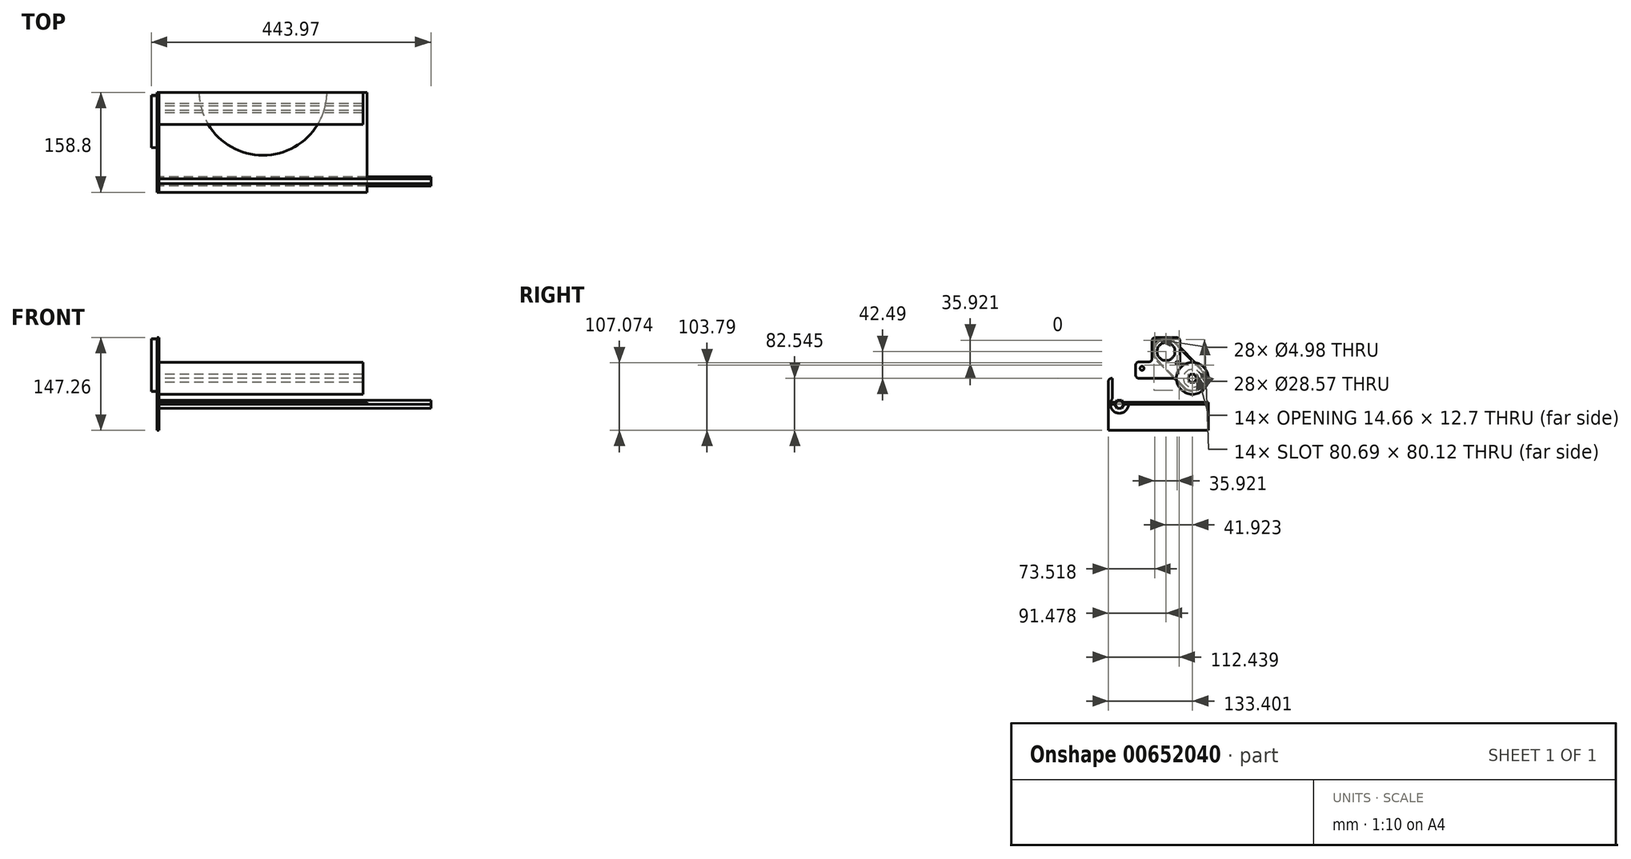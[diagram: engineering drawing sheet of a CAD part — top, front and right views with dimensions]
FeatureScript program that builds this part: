
annotation { "Feature Type Name" : "Feature", "Feature Type Description" : "" }
export const myFeature = defineFeature(function(context is Context, id is Id, definition is map)
    precondition{}
    {
        {
            var Q0;
            Q0=qCreatedBy(makeId("Top.planeOp"),FACE);
            var sketch = newSketch(context, id + "F0", { "sketchPlane" : qUnion([Q0])});
            skLineSegment(sketch, "E0.bottom", {"start": v(-165.1, 82.55) * mm, "end": v(165.1, 82.55) * mm});
            skLineSegment(sketch, "E0.top", {"start": v(-165.1, -82.55) * mm, "end": v(165.1, -82.55) * mm});
            skLineSegment(sketch, "E0.left", {"start": v(-165.1, 82.55) * mm, "end": v(-165.1, -82.55) * mm});
            skLineSegment(sketch, "E0.right", {"start": v(165.1, 82.55) * mm, "end": v(165.1, -82.55) * mm});
            skPoint(sketch, "E0.middle", {"position": v(0, 0) * mm});
            skLineSegment(sketch, "E1.top", {"start": v(-165.1, 31.75) * mm, "end": v(165.1, 31.75) * mm});
            skLineSegment(sketch, "E1.left", {"start": v(-165.1, 82.55) * mm, "end": v(-165.1, 31.75) * mm});
            skLineSegment(sketch, "E1.right", {"start": v(165.1, 82.55) * mm, "end": v(165.1, 31.75) * mm});
            skLineSegment(sketch, "E2.bottom", {"start": v(-165.1, -76.2) * mm, "end": v(-158.75, -76.2) * mm});
            skLineSegment(sketch, "E2.top", {"start": v(-165.1, -47.63) * mm, "end": v(-158.75, -47.63) * mm});
            skLineSegment(sketch, "E2.left", {"start": v(-165.1, -76.2) * mm, "end": v(-165.1, -47.63) * mm});
            skLineSegment(sketch, "E2.right", {"start": v(-158.75, -76.2) * mm, "end": v(-158.75, -47.63) * mm});
            skLineSegment(sketch, "E3", {"start": v(-165.1, 57.15) * mm, "end": v(165.1, 57.15) * mm, "construction": true});
            skLineSegment(sketch, "E4", {"start": v(-165.1, -61.91) * mm, "end": v(165.1, -61.91) * mm, "construction": true});
            skCircle(sketch, "E5", {"center": v(0, 77.79) * mm, "radius": 139.7 * mm, "construction": true});
            skCircle(sketch, "E6", {"center": v(0, 77.79) * mm, "radius": 101.6 * mm});
            skLineSegment(sketch, "E7.bottom", {"start": v(-165.1, 76.25) * mm, "end": v(-147.4, 76.25) * mm});
            skLineSegment(sketch, "E7.top", {"start": v(-165.1, 38.05) * mm, "end": v(-147.4, 38.05) * mm});
            skLineSegment(sketch, "E7.left", {"start": v(-165.1, 76.25) * mm, "end": v(-165.1, 38.05) * mm});
            skLineSegment(sketch, "E7.right", {"start": v(-147.4, 76.25) * mm, "end": v(-147.4, 38.05) * mm});
            skPoint(sketch, "E7.middle", {"position": v(-156.25, 57.15) * mm});
            skLineSegment(sketch, "E8", {"start": v(-165.1, 76.25) * mm, "end": v(165.1, 76.25) * mm});
            skSolve(sketch);
        }
        {
            var Q0;
            {var subQ0=sQuery(id+"F0.wireOp",EDGE,"E7.top");Q0=makeQuery(id+"F0.imprint","IMPRINT",FACE,{"disambiguationData":[TD([[makeQuery(id+"F0.imprint","IMPRINT",EDGE,{"derivedFrom":subQ0}),-1.0]])]});}
            var Q1;
            Q1=makeQuery(id+"F0.imprint","IMPRINT",FACE,{"disambiguationData":[TD([[makeQuery(id+"F0.imprint","IMPRINT",EDGE,{"derivedFrom":sQuery(id+"F0.wireOp",EDGE,"E7.top")}),1.0]])]});
            var Q2;
            {var subQ1=sQuery(id+"F0.wireOp",EDGE,"E1.top");var subQ3=sQuery(id+"F0.wireOp",EDGE,"E6");var subQ4=makeQuery(id+"F0.imprint","INTERSECT",VERTEX,{"disambiguationData":[OD(1.0)],"derivedFrom":[subQ1,subQ3]});Q2=makeQuery(id+"F0.imprint","IMPRINT",FACE,{"disambiguationData":[TD([[makeQuery(id+"F0.imprint","IMPRINT",EDGE,{"disambiguationData":[TD([[subQ4,-1.0]])],"derivedFrom":subQ3}),-1.0]])]});}
            var Q3;
            {var subQ3=sQuery(id+"F0.wireOp",EDGE,"E0.top");Q3=makeQuery(id+"F0.imprint","IMPRINT",FACE,{"disambiguationData":[TD([[makeQuery(id+"F0.imprint","IMPRINT",EDGE,{"derivedFrom":subQ3}),1.0]])]});}
            var Q4;
            Q4=makeQuery(id+"F0.imprint","IMPRINT",FACE,{"disambiguationData":[TD([[makeQuery(id+"F0.imprint","IMPRINT",EDGE,{"derivedFrom":sQuery(id+"F0.wireOp",EDGE,"E2.bottom")}),1.0]])]});
            extrude(context, id + "F1", {"entities" : qUnion([Q0, Q1, Q2, Q3, Q4]), "depth" : 3.17 * mm, "offsetDistance" : 25.4 * mm});
        }
        {
            var Q0;
            Q0=makeQuery(id+"F1.opExtrude","SWEPT_FACE",FACE,{"disambiguationData":[OSD([sQuery(id+"F0.wireOp",EDGE,"E0.left"),sQuery(id+"F0.wireOp",EDGE,"E1.left"),sQuery(id+"F0.wireOp",EDGE,"E2.left")])]});
            var sketch = newSketch(context, id + "F2", { "sketchPlane" : qUnion([Q0])});
            skLineSegment(sketch, "E9.bottom", {"start": v(-76.25, 41.28) * mm, "end": v(76.25, 41.28) * mm});
            skLineSegment(sketch, "E9.top", {"start": v(-76.25, -41.28) * mm, "end": v(76.25, -41.28) * mm});
            skLineSegment(sketch, "E9.left", {"start": v(-76.25, 41.28) * mm, "end": v(-76.25, -41.28) * mm});
            skLineSegment(sketch, "E9.right", {"start": v(76.25, 41.28) * mm, "end": v(76.25, -41.28) * mm});
            skPoint(sketch, "E9.middle", {"position": v(0, 0) * mm});
            skCircle(sketch, "E10", {"center": v(-50.85, 41.28) * mm, "radius": 25.4 * mm});
            skCircle(sketch, "E11", {"center": v(-50.85, 41.28) * mm, "radius": 14.29 * mm});
            skLineSegment(sketch, "E12.bottom", {"start": v(76.25, 41.28) * mm, "end": v(82.55, 41.28) * mm});
            skLineSegment(sketch, "E12.top", {"start": v(76.25, -41.28) * mm, "end": v(82.55, -41.28) * mm});
            skLineSegment(sketch, "E12.left", {"start": v(76.25, 41.27) * mm, "end": v(76.25, -41.28) * mm});
            skLineSegment(sketch, "E12.right", {"start": v(82.55, 41.28) * mm, "end": v(82.55, -41.27) * mm});
            skCircle(sketch, "E13", {"center": v(65.09, 0) * mm, "radius": 14.29 * mm});
            skCircle(sketch, "E14", {"center": v(-8.93, 83.76) * mm, "radius": 25.4 * mm, "construction": true});
            skCircle(sketch, "E15", {"center": v(9.03, 101.73) * mm, "radius": 2.49 * mm});
            skLineSegment(sketch, "E16", {"start": v(-8.93, 83.76) * mm, "end": v(-26.89, 101.73) * mm, "construction": true});
            skLineSegment(sketch, "E17", {"start": v(-8.93, 83.76) * mm, "end": v(9.03, 101.73) * mm, "construction": true});
            skCircle(sketch, "E18.MirrorC", {"center": v(-26.89, 65.8) * mm, "radius": 2.49 * mm});
            skCircle(sketch, "E19", {"center": v(-8.93, 83.76) * mm, "radius": 14.29 * mm});
            skCircle(sketch, "E20", {"center": v(29.17, 57.15) * mm, "radius": 3.18 * mm});
            skLineSegment(sketch, "E21.bottom", {"start": v(13.3, 41.28) * mm, "end": v(45.05, 41.28) * mm});
            skLineSegment(sketch, "E21.top", {"start": v(13.3, 73.02) * mm, "end": v(45.05, 73.02) * mm});
            skLineSegment(sketch, "E21.left", {"start": v(13.3, 41.28) * mm, "end": v(13.3, 73.02) * mm});
            skLineSegment(sketch, "E22", {"start": v(-8.93, 83.76) * mm, "end": v(-8.93, 109.16) * mm, "construction": true});
            skLineSegment(sketch, "E23.bottom", {"start": v(-31.15, 105.99) * mm, "end": v(13.3, 105.99) * mm});
            skLineSegment(sketch, "E23.top", {"start": v(-31.15, 61.54) * mm, "end": v(13.3, 61.54) * mm});
            skLineSegment(sketch, "E23.left", {"start": v(-31.15, 105.99) * mm, "end": v(-31.15, 61.54) * mm});
            skLineSegment(sketch, "E23.right", {"start": v(13.3, 105.99) * mm, "end": v(13.3, 61.54) * mm});
            skLineSegment(sketch, "E24", {"start": v(-31.15, 61.54) * mm, "end": v(-31.15, 41.28) * mm});
            skLineSegment(sketch, "E25", {"start": v(13.3, 73.02) * mm, "end": v(13.3, 61.54) * mm});
            skLineSegment(sketch, "E26", {"start": v(13.3, 67.28) * mm, "end": v(39.3, 67.28) * mm});
            skLineSegment(sketch, "E27", {"start": v(39.3, 67.28) * mm, "end": v(39.3, 41.28) * mm});
            skSolve(sketch);
        }
        {
            var Q0;
            {var subQ11=sQuery(id+"F2.wireOp",EDGE,"qfJLn3O9-GlWD-lMOJ-bS2u-81kLyVJAWFBw.top");Q0=makeQuery(id+"F2.imprint","IMPRINT",FACE,{"disambiguationData":[TD([[makeQuery(id+"F2.imprint","IMPRINT",EDGE,{"derivedFrom":subQ11}),-1.0]])]});}
            var Q1;
            {var subQ0=sQuery(id+"F2.wireOp",EDGE,"E10");var subQ1=sQuery(id+"F2.wireOp",EDGE,"E9.bottom");var subQ5=makeQuery(id+"F2.imprint","INTERSECT",VERTEX,{"derivedFrom":[subQ1,subQ0]});Q1=makeQuery(id+"F2.imprint","IMPRINT",FACE,{"disambiguationData":[TD([[makeQuery(id+"F2.imprint","IMPRINT",EDGE,{"disambiguationData":[TD([[subQ5,1.0]])],"derivedFrom":subQ1}),-1.0]])]});}
            var Q2;
            {var subQ0=sQuery(id+"F2.wireOp",EDGE,"E10");var subQ1=sQuery(id+"F2.wireOp",EDGE,"E9.bottom");var subQ5=makeQuery(id+"F2.imprint","INTERSECT",VERTEX,{"derivedFrom":[subQ1,subQ0]});Q2=makeQuery(id+"F2.imprint","IMPRINT",FACE,{"disambiguationData":[TD([[makeQuery(id+"F2.imprint","IMPRINT",EDGE,{"disambiguationData":[TD([[subQ5,1.0]])],"derivedFrom":subQ1}),1.0]])]});}
            var Q3;
            {var subQ5=sQuery(id+"F2.wireOp",EDGE,"E9.top");Q3=makeQuery(id+"F2.imprint","IMPRINT",FACE,{"disambiguationData":[TD([[makeQuery(id+"F2.imprint","IMPRINT",EDGE,{"derivedFrom":subQ5}),1.0]])]});}
            var Q4;
            {var subQ5=sQuery(id+"F2.wireOp",EDGE,"E12.bottom");Q4=makeQuery(id+"F2.imprint","IMPRINT",FACE,{"disambiguationData":[TD([[makeQuery(id+"F2.imprint","IMPRINT",EDGE,{"derivedFrom":subQ5}),-1.0]])]});}
            var Q5;
            {var subQ7=sQuery(id+"F2.wireOp",EDGE,"E12.top");Q5=makeQuery(id+"F2.imprint","IMPRINT",FACE,{"disambiguationData":[TD([[makeQuery(id+"F2.imprint","IMPRINT",EDGE,{"derivedFrom":subQ7}),1.0]])]});}
            var Q6;
            Q6=makeQuery(id+"F2.imprint","IMPRINT",FACE,{"disambiguationData":[TD([[makeQuery(id+"F2.imprint","IMPRINT",EDGE,{"derivedFrom":sQuery(id+"F2.wireOp",EDGE,"E20")}),-1.0]])]});
            var Q7;
            {var subQ3=sQuery(id+"F2.wireOp",EDGE,"E21.left");Q7=makeQuery(id+"F2.imprint","IMPRINT",FACE,{"disambiguationData":[TD([[makeQuery(id+"F2.imprint","IMPRINT",EDGE,{"derivedFrom":subQ3}),1.0]])]});}
            var Q8;
            {var subQ1=sQuery(id+"F2.wireOp",EDGE,"qfJLn3O9-GlWD-lMOJ-bS2u-81kLyVJAWFBw.bottom");Q8=makeQuery(id+"F2.imprint","IMPRINT",FACE,{"disambiguationData":[TD([[makeQuery(id+"F2.imprint","IMPRINT",EDGE,{"derivedFrom":subQ1}),-1.0]])]});}
            var Q9;
            {var subQ0=sQuery(id+"F2.wireOp",EDGE,"E9.left");var subQ1=sQuery(id+"F0.wireOp",EDGE,"E7.left");var subQ2=sQuery(id+"F0.wireOp",EDGE,"E2.left");var subQ3=sQuery(id+"F0.wireOp",EDGE,"E1.left");var subQ4=sQuery(id+"F0.wireOp",EDGE,"E0.left");var subQ5=makeQuery(id+"F1.opExtrude","CAP_EDGE",EDGE,{"disambiguationData":[OSD([subQ4,subQ3,subQ2,subQ1])],"isStart":true});var subQ6=makeQuery(id+"F2.imprint","INTERSECT",VERTEX,{"derivedFrom":[subQ5,subQ0]});Q9=makeQuery(id+"F2.imprint","IMPRINT",FACE,{"disambiguationData":[TD([[makeQuery(id+"F2.imprint","IMPRINT",EDGE,{"disambiguationData":[TD([[subQ6,1.0]])],"derivedFrom":subQ0}),1.0]])]});}
            var Q10;
            {var subQ0=sQuery(id+"F2.wireOp",EDGE,"E12.right");var subQ1=sQuery(id+"F0.wireOp",EDGE,"E7.left");var subQ2=sQuery(id+"F0.wireOp",EDGE,"E2.left");var subQ3=sQuery(id+"F0.wireOp",EDGE,"E1.left");var subQ4=sQuery(id+"F0.wireOp",EDGE,"E0.left");var subQ5=makeQuery(id+"F1.opExtrude","CAP_EDGE",EDGE,{"disambiguationData":[OSD([subQ4,subQ3,subQ2,subQ1])],"isStart":true});var subQ6=makeQuery(id+"F2.imprint","INTERSECT",VERTEX,{"derivedFrom":[subQ5,subQ0]});Q10=makeQuery(id+"F2.imprint","IMPRINT",FACE,{"disambiguationData":[TD([[makeQuery(id+"F2.imprint","IMPRINT",EDGE,{"disambiguationData":[TD([[subQ6,1.0]])],"derivedFrom":subQ0}),-1.0]])]});}
            var Q11;
            Q11=makeQuery(id+"F2.imprint","IMPRINT",FACE,{"disambiguationData":[TD([[makeQuery(id+"F2.imprint","IMPRINT",EDGE,{"derivedFrom":sQuery(id+"F2.wireOp",EDGE,"E15")}),-1.0]])]});
            var Q12;
            {var subQ8=sQuery(id+"F2.wireOp",EDGE,"E21.bottom");Q12=makeQuery(id+"F2.imprint","IMPRINT",FACE,{"disambiguationData":[TD([[makeQuery(id+"F2.imprint","IMPRINT",EDGE,{"derivedFrom":subQ8}),-1.0]])]});}
            var Q13;
            {var subQ1=sQuery(id+"F2.wireOp",EDGE,"E9.bottom");var subQ4=sQuery(id+"F2.wireOp",EDGE,"E24");var subQ5=makeQuery(id+"F2.imprint","INTERSECT",VERTEX,{"derivedFrom":[subQ1,subQ4]});Q13=makeQuery(id+"F2.imprint","IMPRINT",FACE,{"disambiguationData":[TD([[makeQuery(id+"F2.imprint","IMPRINT",EDGE,{"disambiguationData":[TD([[subQ5,1.0]])],"derivedFrom":subQ1}),1.0]])]});}
            extrude(context, id + "F3", {"entities" : qUnion([Q0, Q1, Q2, Q3, Q4, Q5, Q6, Q7, Q8, Q9, Q10, Q11, Q12, Q13]), "depth" : 3.17 * mm, "offsetDistance" : 25.4 * mm});
        }
        {
            var Q0;
            Q0=makeQuery(id+"F3.opExtrude","CAP_FACE",FACE,{"disambiguationData":[OSD([sQuery(id+"F2.wireOp",EDGE,"E9.bottom"),sQuery(id+"F2.wireOp",EDGE,"E9.top"),sQuery(id+"F2.wireOp",EDGE,"E9.left"),sQuery(id+"F2.wireOp",EDGE,"E10"),sQuery(id+"F2.wireOp",EDGE,"E11"),sQuery(id+"F2.wireOp",EDGE,"E12.bottom"),sQuery(id+"F2.wireOp",EDGE,"E12.top"),sQuery(id+"F2.wireOp",EDGE,"E12.right"),sQuery(id+"F2.wireOp",EDGE,"E13"),sQuery(id+"F2.wireOp",EDGE,"qfJLn3O9-GlWD-lMOJ-bS2u-81kLyVJAWFBw.bottom"),sQuery(id+"F2.wireOp",EDGE,"qfJLn3O9-GlWD-lMOJ-bS2u-81kLyVJAWFBw.left"),sQuery(id+"F2.wireOp",EDGE,"qfJLn3O9-GlWD-lMOJ-bS2u-81kLyVJAWFBw.right"),sQuery(id+"F2.wireOp",EDGE,"E15"),sQuery(id+"F2.wireOp",EDGE,"E18.MirrorC"),sQuery(id+"F2.wireOp",EDGE,"E19"),sQuery(id+"F2.wireOp",EDGE,"E20"),sQuery(id+"F2.wireOp",EDGE,"E21.top"),sQuery(id+"F2.wireOp",EDGE,"E21.right"),sQuery(id+"F2.wireOp",EDGE,"WHWuN5Ua-Tlyi-y9Cq-qCwo-jjhaEeOhI5ko")])],"isStart":true});
            var sketch = newSketch(context, id + "F4", { "sketchPlane" : qUnion([Q0])});
            skCircle(sketch, "E28", {"center": v(50.85, 41.28) * mm, "radius": 25.4 * mm});
            skCircle(sketch, "E29.cCircle", {"center": v(50.85, 41.28) * mm, "radius": 6.35 * mm, "construction": true});
            skLineSegment(sketch, "E29.0", {"start": v(47.18, 47.63) * mm, "end": v(54.52, 47.63) * mm});
            skLineSegment(sketch, "E29.1", {"start": v(54.52, 47.63) * mm, "end": v(58.18, 41.27) * mm});
            skLineSegment(sketch, "E29.2", {"start": v(58.18, 41.27) * mm, "end": v(54.52, 34.92) * mm});
            skLineSegment(sketch, "E29.3", {"start": v(54.52, 34.93) * mm, "end": v(47.18, 34.93) * mm});
            skLineSegment(sketch, "E29.4", {"start": v(47.18, 34.93) * mm, "end": v(43.52, 41.28) * mm});
            skLineSegment(sketch, "E29.5", {"start": v(43.52, 41.28) * mm, "end": v(47.18, 47.63) * mm});
            skPoint(sketch, "E29.0.midPoint", {"position": v(50.85, 47.62) * mm});
            skCircle(sketch, "E30.cCircle", {"center": v(-65.09, 0) * mm, "radius": 6.35 * mm, "construction": true});
            skLineSegment(sketch, "E30.0", {"start": v(-68.75, 6.35) * mm, "end": v(-61.42, 6.35) * mm});
            skLineSegment(sketch, "E30.1", {"start": v(-61.42, 6.35) * mm, "end": v(-57.76, 0) * mm});
            skLineSegment(sketch, "E30.2", {"start": v(-57.76, 0) * mm, "end": v(-61.42, -6.35) * mm});
            skLineSegment(sketch, "E30.3", {"start": v(-61.42, -6.35) * mm, "end": v(-68.75, -6.35) * mm});
            skLineSegment(sketch, "E30.4", {"start": v(-68.75, -6.35) * mm, "end": v(-72.42, 0) * mm});
            skLineSegment(sketch, "E30.5", {"start": v(-72.42, 0) * mm, "end": v(-68.75, 6.35) * mm});
            skPoint(sketch, "E30.0.midPoint", {"position": v(-65.09, 6.35) * mm});
            skSolve(sketch);
        }
        {
            var Q0;
            Q0=makeQuery(id+"F4.imprint","IMPRINT",FACE,{"disambiguationData":[TD([[makeQuery(id+"F4.imprint","IMPRINT",EDGE,{"derivedFrom":makeQuery(id+"F3.opExtrude","CAP_EDGE",EDGE,{"disambiguationData":[OSD([sQuery(id+"F2.wireOp",EDGE,"W6DhLB1R-Bibj-mR2K-u9WB-GpnqnpVcpbQg")])],"isStart":true})}),1.0]])]});
            var Q1;
            Q1=makeQuery(id+"F4.imprint","IMPRINT",FACE,{"disambiguationData":[TD([[makeQuery(id+"F4.imprint","IMPRINT",EDGE,{"derivedFrom":sQuery(id+"F4.wireOp",EDGE,"E29.0")}),1.0]])]});
            var Q2;
            {var subQ5=makeQuery(id+"F3.opExtrude","CAP_EDGE",EDGE,{"disambiguationData":[OSD([sQuery(id+"F2.wireOp",EDGE,"qPiBjacE-2YdZ-56Vs-2SOP-qVqnwwztWqQn")])],"isStart":true});Q2=makeQuery(id+"F4.imprint","IMPRINT",FACE,{"disambiguationData":[TD([[makeQuery(id+"F4.imprint","IMPRINT",EDGE,{"derivedFrom":subQ5}),1.0]])]});}
            var Q3;
            {var subQ0=sQuery(id+"F4.wireOp",EDGE,"E28");Q3=makeQuery(id+"F4.imprint","IMPRINT",FACE,{"disambiguationData":[TD([[makeQuery(id+"F4.imprint","IMPRINT",EDGE,{"disambiguationData":[OD(0.0)],"derivedFrom":subQ0}),-1.0]])]});}
            extrude(context, id + "F5", {"entities" : qUnion([Q0, Q1, Q2, Q3]), "depth" : 323.85 * mm, "offsetDistance" : 25.4 * mm});
        }
        {
            var Q0;
            Q0=makeQuery(id+"F4.imprint","IMPRINT",FACE,{"disambiguationData":[TD([[makeQuery(id+"F4.imprint","IMPRINT",EDGE,{"derivedFrom":sQuery(id+"F4.wireOp",EDGE,"E30.0")}),-1.0]])]});
            extrude(context, id + "F6", {"entities" : qUnion([Q0]), "depth" : 431.8 * mm, "offsetDistance" : 25.4 * mm});
        }
        {
            var Q0;
            Q0=makeQuery(id+"F3.opExtrude","CAP_FACE",FACE,{"disambiguationData":[OSD([sQuery(id+"F2.wireOp",EDGE,"E9.bottom"),sQuery(id+"F2.wireOp",EDGE,"E9.top"),sQuery(id+"F2.wireOp",EDGE,"E9.left"),sQuery(id+"F2.wireOp",EDGE,"E10"),sQuery(id+"F2.wireOp",EDGE,"E11"),sQuery(id+"F2.wireOp",EDGE,"E12.bottom"),sQuery(id+"F2.wireOp",EDGE,"E12.top"),sQuery(id+"F2.wireOp",EDGE,"E12.right"),sQuery(id+"F2.wireOp",EDGE,"E13"),sQuery(id+"F2.wireOp",EDGE,"E15"),sQuery(id+"F2.wireOp",EDGE,"E18.MirrorC"),sQuery(id+"F2.wireOp",EDGE,"E19"),sQuery(id+"F2.wireOp",EDGE,"E20"),sQuery(id+"F2.wireOp",EDGE,"E21.top"),sQuery(id+"F2.wireOp",EDGE,"E21.right"),sQuery(id+"F2.wireOp",EDGE,"E23.bottom"),sQuery(id+"F2.wireOp",EDGE,"E23.left"),sQuery(id+"F2.wireOp",EDGE,"E23.right"),sQuery(id+"F2.wireOp",EDGE,"E24")])],"isStart":false});
            var sketch = newSketch(context, id + "F7", { "sketchPlane" : qUnion([Q0])});
            skCircle(sketch, "E31.0", {"center": v(29.17, 57.15) * mm, "radius": 3.18 * mm});
            skPoint(sketch, "E32.0", {"position": v(13.3, 41.28) * mm});
            skArc(sketch, "E33", {"start": v(-64.45, 54.7) * mm, "mid": v(-64.27, 27.68) * mm, "end": v(-37.25, 27.86) * mm});
            skArc(sketch, "E34", {"start": v(4.67, 70.35) * mm, "mid": v(4.49, 97.36) * mm, "end": v(-22.52, 97.18) * mm});
            skLineSegment(sketch, "E35", {"start": v(-64.45, 54.7) * mm, "end": v(-22.52, 97.18) * mm});
            skLineSegment(sketch, "E36", {"start": v(-37.25, 27.86) * mm, "end": v(4.67, 70.35) * mm});
            skLineSegment(sketch, "E37.0", {"start": v(-65.59, 55.81) * mm, "end": v(-23.66, 98.3) * mm});
            skArc(sketch, "E38", {"start": v(-65.59, 55.81) * mm, "mid": v(-65.39, 26.54) * mm, "end": v(-36.11, 26.74) * mm});
            skArc(sketch, "E39", {"start": v(5.8, 69.23) * mm, "mid": v(5.61, 98.5) * mm, "end": v(-23.66, 98.3) * mm});
            skLineSegment(sketch, "E40.0", {"start": v(-36.11, 26.74) * mm, "end": v(5.8, 69.23) * mm});
            skSolve(sketch);
        }
        {
            var Q0;
            {var subQ10=sQuery(id+"F7.wireOp",EDGE,"E33");Q0=makeQuery(id+"F7.imprint","IMPRINT",FACE,{"disambiguationData":[TD([[makeQuery(id+"F7.imprint","IMPRINT",EDGE,{"derivedFrom":subQ10}),-1.0]])]});}
            var Q1;
            {var subQ1=makeQuery(id+"F3.opExtrude","CAP_EDGE",EDGE,{"disambiguationData":[OSD([sQuery(id+"F2.wireOp",EDGE,"E10")])],"isStart":false});var subQ5=sQuery(id+"F7.wireOp",EDGE,"E37.0");var subQ6=makeQuery(id+"F7.imprint","INTERSECT",VERTEX,{"derivedFrom":[subQ1,subQ5]});Q1=makeQuery(id+"F7.imprint","IMPRINT",FACE,{"disambiguationData":[TD([[makeQuery(id+"F7.imprint","IMPRINT",EDGE,{"disambiguationData":[TD([[subQ6,1.0]])],"derivedFrom":subQ1}),-1.0]])]});}
            extrude(context, id + "F8", {"entities" : qUnion([Q0, Q1]), "depth" : 9 * mm, "offsetDistance" : 25.4 * mm});
        }
        {
            var Q0;
            Q0=makeQuery(id+"F3.opExtrude","SWEPT_EDGE",EDGE,{"disambiguationData":[OSD([sQuery(id+"F2.wireOp",EDGE,"E9.bottom"),sQuery(id+"F2.wireOp",EDGE,"E10")])]});
            var Q1;
            Q1=makeQuery(id+"F3.opExtrude","SWEPT_EDGE",EDGE,{"disambiguationData":[OSD([sQuery(id+"F2.wireOp",EDGE,"E9.bottom"),sQuery(id+"F2.wireOp",EDGE,"qfJLn3O9-GlWD-lMOJ-bS2u-81kLyVJAWFBw.top"),sQuery(id+"F2.wireOp",EDGE,"qfJLn3O9-GlWD-lMOJ-bS2u-81kLyVJAWFBw.left")])]});
            var Q2;
            Q2=makeQuery(id+"F3.opExtrude","SWEPT_EDGE",EDGE,{"disambiguationData":[OSD([sQuery(id+"F2.wireOp",EDGE,"qfJLn3O9-GlWD-lMOJ-bS2u-81kLyVJAWFBw.bottom"),sQuery(id+"F2.wireOp",EDGE,"qfJLn3O9-GlWD-lMOJ-bS2u-81kLyVJAWFBw.left")])]});
            var Q3;
            Q3=makeQuery(id+"F3.opExtrude","SWEPT_EDGE",EDGE,{"disambiguationData":[OSD([sQuery(id+"F2.wireOp",EDGE,"qfJLn3O9-GlWD-lMOJ-bS2u-81kLyVJAWFBw.bottom"),sQuery(id+"F2.wireOp",EDGE,"qfJLn3O9-GlWD-lMOJ-bS2u-81kLyVJAWFBw.right")])]});
            var Q4;
            Q4=makeQuery(id+"F3.opExtrude","SWEPT_EDGE",EDGE,{"disambiguationData":[OSD([sQuery(id+"F2.wireOp",EDGE,"qfJLn3O9-GlWD-lMOJ-bS2u-81kLyVJAWFBw.right"),sQuery(id+"F2.wireOp",EDGE,"WHWuN5Ua-Tlyi-y9Cq-qCwo-jjhaEeOhI5ko")])]});
            var Q5;
            Q5=makeQuery(id+"F3.opExtrude","SWEPT_EDGE",EDGE,{"disambiguationData":[OSD([sQuery(id+"F2.wireOp",EDGE,"E21.top"),sQuery(id+"F2.wireOp",EDGE,"E21.right")])]});
            var Q6;
            Q6=makeQuery(id+"F3.opExtrude","SWEPT_EDGE",EDGE,{"disambiguationData":[OSD([sQuery(id+"F2.wireOp",EDGE,"E9.bottom"),sQuery(id+"F2.wireOp",EDGE,"E21.bottom"),sQuery(id+"F2.wireOp",EDGE,"E21.right")])]});
            var Q7;
            Q7=makeQuery(id+"F3.opExtrude","SWEPT_EDGE",EDGE,{"disambiguationData":[OSD([sQuery(id+"F2.wireOp",EDGE,"E12.bottom"),sQuery(id+"F2.wireOp",EDGE,"E12.right")])]});
            var Q8;
            Q8=makeQuery(id+"F3.opExtrude","SWEPT_EDGE",EDGE,{"disambiguationData":[OSD([sQuery(id+"F2.wireOp",EDGE,"E26"),sQuery(id+"F2.wireOp",EDGE,"E27")])]});
            var Q9;
            Q9=makeQuery(id+"F3.opExtrude","SWEPT_EDGE",EDGE,{"disambiguationData":[OSD([sQuery(id+"F2.wireOp",EDGE,"E25"),sQuery(id+"F2.wireOp",EDGE,"E26")])]});
            var Q10;
            Q10=makeQuery(id+"F3.opExtrude","SWEPT_EDGE",EDGE,{"disambiguationData":[OSD([sQuery(id+"F2.wireOp",EDGE,"E23.bottom"),sQuery(id+"F2.wireOp",EDGE,"E23.right")])]});
            var Q11;
            Q11=makeQuery(id+"F3.opExtrude","SWEPT_EDGE",EDGE,{"disambiguationData":[OSD([sQuery(id+"F2.wireOp",EDGE,"E23.bottom"),sQuery(id+"F2.wireOp",EDGE,"E23.left")])]});
            var Q12;
            Q12=makeQuery(id+"F3.opExtrude","SWEPT_EDGE",EDGE,{"disambiguationData":[OSD([sQuery(id+"F2.wireOp",EDGE,"E10"),sQuery(id+"F2.wireOp",EDGE,"E24")])]});
            fillet(context, id + "F9", {"entities" : qUnion([Q0, Q1, Q2, Q3, Q4, Q5, Q6, Q7, Q8, Q9, Q10, Q11, Q12]), "radius" : 5.08 * mm, "tangentPropagation" : true, "allowEdgeOverflow" : false});
        }
    });
